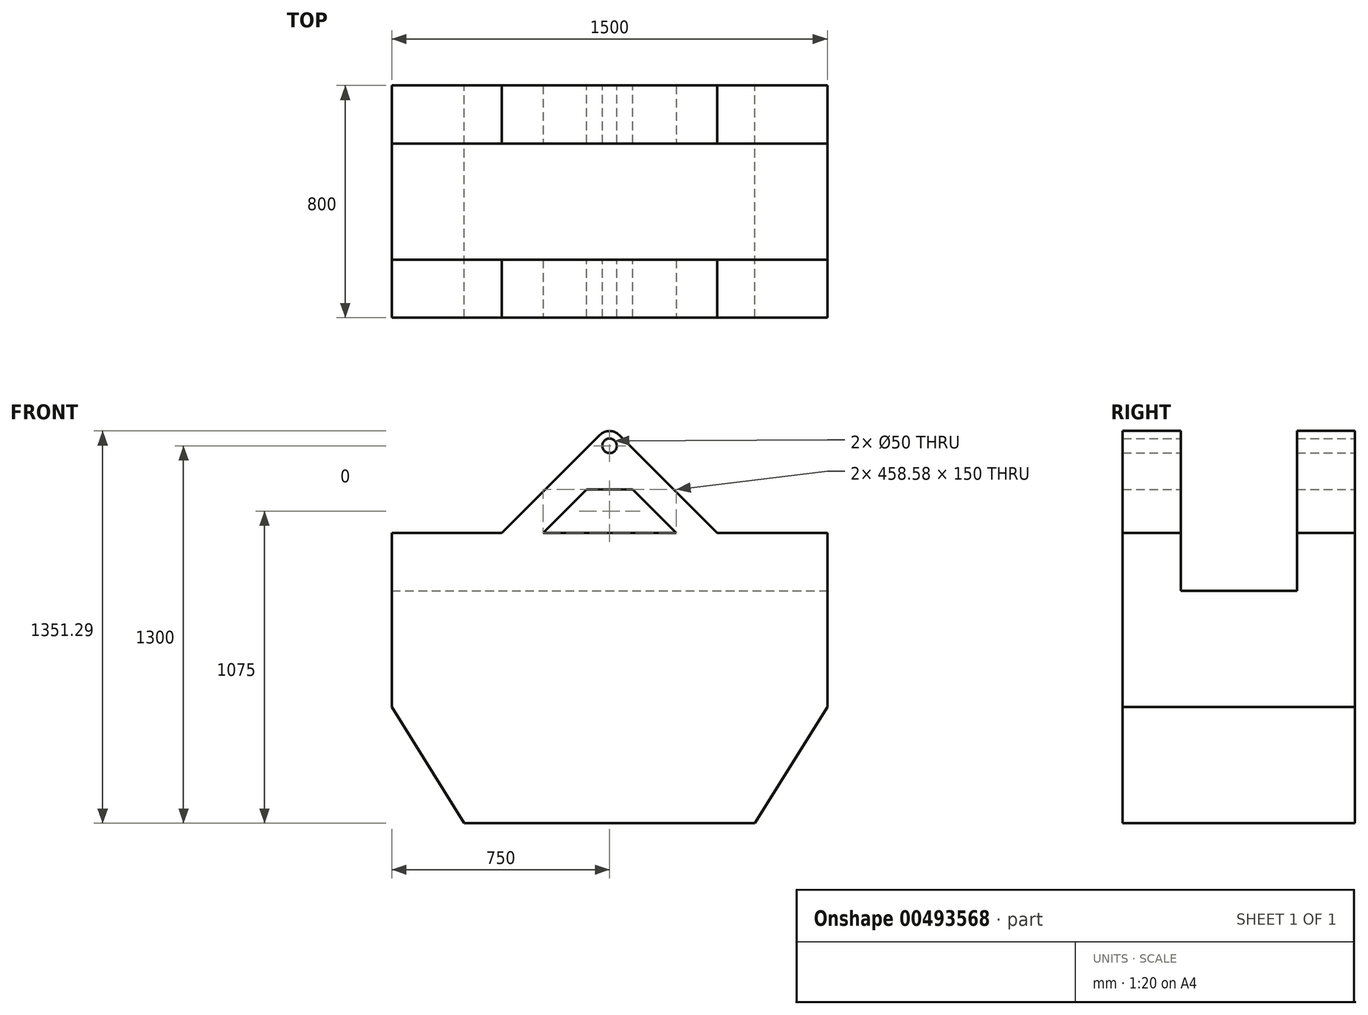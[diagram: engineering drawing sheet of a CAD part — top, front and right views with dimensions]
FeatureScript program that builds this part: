
annotation { "Feature Type Name" : "Feature", "Feature Type Description" : "" }
export const myFeature = defineFeature(function(context is Context, id is Id, definition is map)
    precondition{}
    {
        {
            var Q0;
            Q0=qCreatedBy(makeId("Front.planeOp"),FACE);
            var sketch = newSketch(context, id + "F0", { "sketchPlane" : qUnion([Q0])});
            skLineSegment(sketch, "E0", {"start": v(-750, 0) * mm, "end": v(750, 0) * mm});
            skLineSegment(sketch, "E1", {"start": v(750, 0) * mm, "end": v(750, -600) * mm});
            skLineSegment(sketch, "E2", {"start": v(750, -600) * mm, "end": v(500, -1000) * mm});
            skLineSegment(sketch, "E3", {"start": v(500, -1000) * mm, "end": v(-500, -1000) * mm});
            skLineSegment(sketch, "E4", {"start": v(-500, -1000) * mm, "end": v(-750, -600) * mm});
            skLineSegment(sketch, "E5", {"start": v(-750, -600) * mm, "end": v(-750, 0) * mm});
            skSolve(sketch);
        }
        {
            var Q0;
            Q0 = qSketchRegion(id + "F0", true);
            extrude(context, id + "F1", {"entities" : qUnion([Q0]), "endBound" : BoundingType.SYMMETRIC, "depth" : 800 * mm});
        }
        {
            var Q0;
            Q0=qCreatedBy(makeId("Front.planeOp"),FACE);
            var sketch = newSketch(context, id + "F2", { "sketchPlane" : qUnion([Q0])});
            skPoint(sketch, "E6", {"position": v(0, 300) * mm});
            skLineSegment(sketch, "E7", {"start": v(0, 304.39) * mm, "end": v(0, -236.08) * mm, "construction": true});
            skLineSegment(sketch, "E8", {"start": v(-300, 236.49) * mm, "end": v(-300, -301.27) * mm, "construction": true});
            skLineSegment(sketch, "E9", {"start": v(300, 255.5) * mm, "end": v(300, -350.15) * mm, "construction": true});
            skLineSegment(sketch, "E10", {"start": v(0, 300) * mm, "end": v(-300, 0) * mm, "construction": true});
            skLineSegment(sketch, "E11", {"start": v(0, 304.39) * mm, "end": v(300, 0) * mm, "construction": true});
            skLineSegment(sketch, "E12", {"start": v(-455.4, -84.7) * mm, "end": v(-32.92, 337.79) * mm});
            skPoint(sketch, "E13", {"position": v(-424.35, -124.18) * mm});
            skLineSegment(sketch, "E14.MirrorCS", {"start": v(-386.47, -157.19) * mm, "end": v(-79.29, 150) * mm});
            skArc(sketch, "E15", {"start": v(-386.47, -157.19) * mm, "mid": v(-460.76, -158.8) * mm, "end": v(-455.4, -84.7) * mm});
            skLineSegment(sketch, "E16", {"start": v(0, 150) * mm, "end": v(-79.29, 150) * mm});
            skLineSegment(sketch, "E17.MirrorCS", {"start": v(0, 150) * mm, "end": v(79.29, 150) * mm});
            skLineSegment(sketch, "E18.MirrorCS", {"start": v(455.4, -84.7) * mm, "end": v(32.92, 337.79) * mm});
            skLineSegment(sketch, "E19.MirrorCS", {"start": v(386.47, -157.19) * mm, "end": v(79.29, 150) * mm});
            skArc(sketch, "E20.MirrorCS", {"start": v(386.47, -157.19) * mm, "mid": v(460.76, -158.8) * mm, "end": v(455.4, -84.7) * mm});
            skPoint(sketch, "E21.trimOffspring.end.orphan", {"position": v(-37.79, 267.08) * mm});
            skPoint(sketch, "E22.trimOffspring.end.orphan", {"position": v(37.79, 267.08) * mm});
            skArc(sketch, "E23", {"start": v(-32.92, 337.79) * mm, "mid": v(0, 351.29) * mm, "end": v(32.92, 337.79) * mm});
            skCircle(sketch, "E24", {"center": v(0, 300) * mm, "radius": 25 * mm});
            skSolve(sketch);
        }
        {
            var Q0;
            Q0 = qSketchRegion(id + "F2", true);
            extrude(context, id + "F3", {"entities" : qUnion([Q0]), "operationType" : NewBodyOperationType.ADD, "endBound" : BoundingType.SYMMETRIC, "depth" : 800 * mm});
        }
        {
            var Q0;
            Q0=makeQuery(id+"F1.opExtrude","SWEPT_FACE",FACE,{"disambiguationData":[OSD([sQuery(id+"F0.wireOp",EDGE,"E1")])]});
            var sketch = newSketch(context, id + "F4", { "sketchPlane" : qUnion([Q0])});
            skLineSegment(sketch, "E25.bottom", {"start": v(-200, 500) * mm, "end": v(200, 500) * mm});
            skLineSegment(sketch, "E25.left", {"start": v(-200, 500) * mm, "end": v(-200, 0) * mm});
            skLineSegment(sketch, "E25.right", {"start": v(200, 500) * mm, "end": v(200, 0) * mm});
            skLineSegment(sketch, "E26.top", {"start": v(-200, -200) * mm, "end": v(200, -200) * mm});
            skLineSegment(sketch, "E26.left", {"start": v(-200, 0) * mm, "end": v(-200, -200) * mm});
            skLineSegment(sketch, "E26.right", {"start": v(200, 0) * mm, "end": v(200, -200) * mm});
            skSolve(sketch);
        }
        {
            var Q0;
            Q0 = qSketchRegion(id + "F4", true);
            extrude(context, id + "F5", {"entities" : qUnion([Q0]), "operationType" : NewBodyOperationType.REMOVE, "oppositeDirection" : true, "depth" : 1500 * mm});
        }
    });
